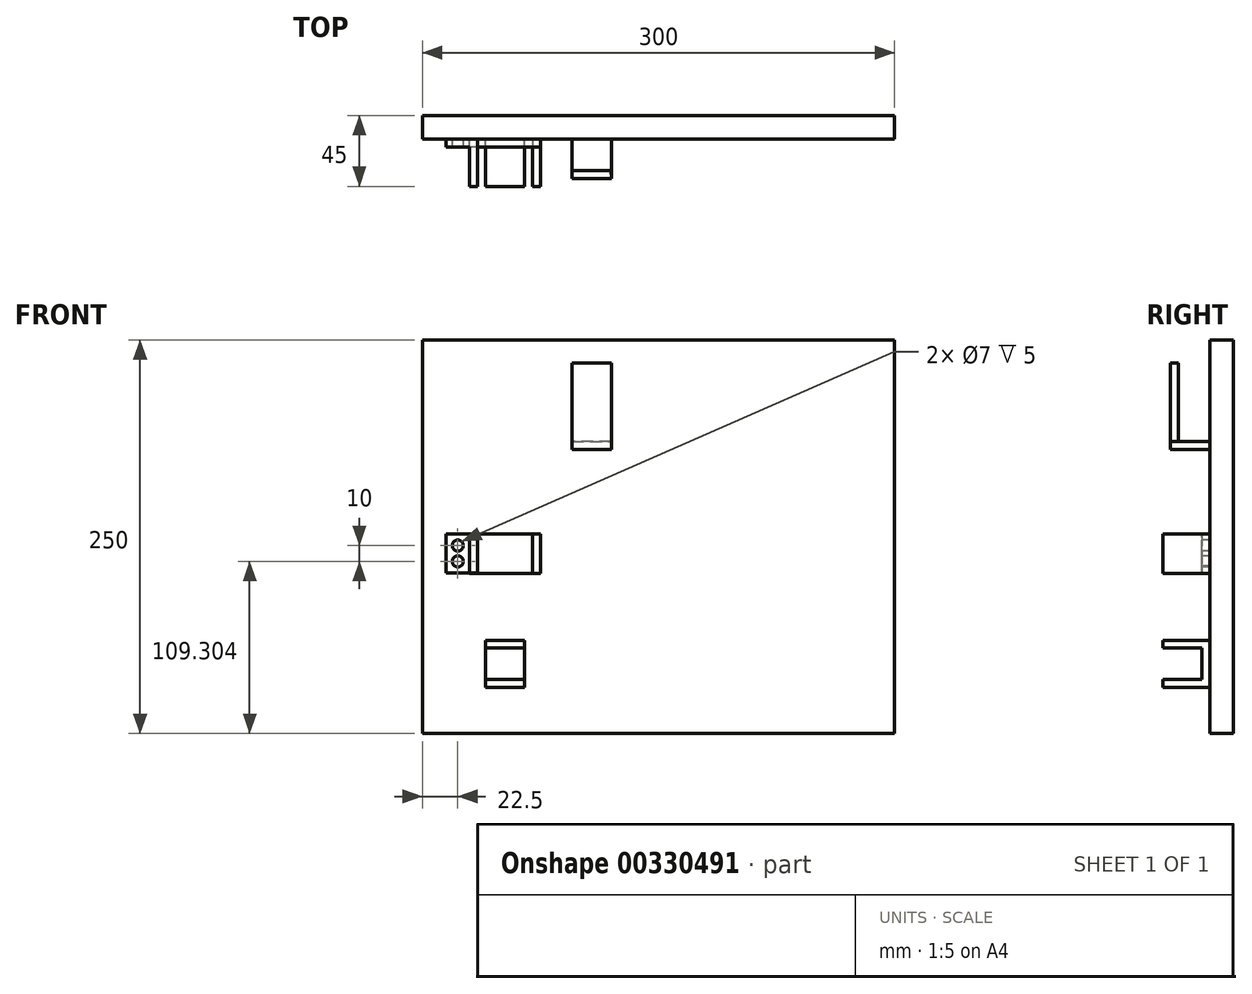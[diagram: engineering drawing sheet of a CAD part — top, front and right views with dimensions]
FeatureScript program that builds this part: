
annotation { "Feature Type Name" : "Feature", "Feature Type Description" : "" }
export const myFeature = defineFeature(function(context is Context, id is Id, definition is map)
    precondition{}
    {
        {
            var Q0;
            Q0=qCreatedBy(makeId("Front.planeOp"),FACE);
            var sketch = newSketch(context, id + "F0", { "sketchPlane" : qUnion([Q0])});
            skLineSegment(sketch, "E0", {"start": v(0, 0) * mm, "end": v(300, 0) * mm});
            skLineSegment(sketch, "E1", {"start": v(300, 0) * mm, "end": v(300, -250) * mm});
            skLineSegment(sketch, "E2", {"start": v(300, -250) * mm, "end": v(0, -250) * mm});
            skLineSegment(sketch, "E3", {"start": v(0, -250) * mm, "end": v(0, 0) * mm});
            skSolve(sketch);
        }
        {
            var Q0;
            Q0=makeQuery(id+"F0.imprint","IMPRINT",FACE,{"disambiguationData":[TD([[makeQuery(id+"F0.imprint","IMPRINT",EDGE,{"derivedFrom":sQuery(id+"F0.wireOp",EDGE,"E0")}),-1.0]])]});
            extrude(context, id + "F1", {"entities" : qUnion([Q0]), "oppositeDirection" : true, "depth" : 15 * mm});
        }
        {
            var Q0;
            Q0=qCreatedBy(makeId("Front.planeOp"),FACE);
            var sketch = newSketch(context, id + "F2", { "sketchPlane" : qUnion([Q0])});
            skLineSegment(sketch, "E4", {"start": v(40.68, -249.67) * mm, "end": v(40.68, -148.2) * mm, "construction": true});
            skLineSegment(sketch, "E5", {"start": v(40.68, -148.2) * mm, "end": v(0, -148.2) * mm, "construction": true});
            skLineSegment(sketch, "E6", {"start": v(0, -148.2) * mm, "end": v(30, -148.2) * mm, "construction": true});
            skLineSegment(sketch, "E7", {"start": v(30, -148.2) * mm, "end": v(105, -148.2) * mm, "construction": true});
            skLineSegment(sketch, "E8", {"start": v(30, -148.2) * mm, "end": v(15, -148.2) * mm});
            skLineSegment(sketch, "E9", {"start": v(15, -148.2) * mm, "end": v(15, -123.2) * mm});
            skLineSegment(sketch, "E10", {"start": v(15, -123.2) * mm, "end": v(30, -123.2) * mm});
            skLineSegment(sketch, "E11", {"start": v(30, -123.2) * mm, "end": v(30, -148.2) * mm});
            skSolve(sketch);
        }
        {
            var Q0;
            Q0 = qSketchRegion(id + "F2", true);
            extrude(context, id + "F3", {"entities" : qUnion([Q0]), "operationType" : NewBodyOperationType.ADD, "depth" : 5 * mm});
        }
        {
            var Q0;
            Q0=makeQuery(id+"F3.opExtrude","CAP_FACE",FACE,{"disambiguationData":[OSD([sQuery(id+"F2.wireOp",EDGE,"E8"),sQuery(id+"F2.wireOp",EDGE,"E9"),sQuery(id+"F2.wireOp",EDGE,"E10"),sQuery(id+"F2.wireOp",EDGE,"E11")])],"isStart":false});
            var sketch = newSketch(context, id + "F4", { "sketchPlane" : qUnion([Q0])});
            skPoint(sketch, "E12.endSnap0", {"position": v(22.5, -123.2) * mm});
            skPoint(sketch, "E12.end.orphan", {"position": v(22.5, -138.2) * mm});
            skPoint(sketch, "E12.start.orphan", {"position": v(22.5, -148.2) * mm});
            skCircle(sketch, "E13", {"center": v(22.5, -130.7) * mm, "radius": 3.5 * mm});
            skCircle(sketch, "E14", {"center": v(22.5, -140.7) * mm, "radius": 3.5 * mm});
            skSolve(sketch);
        }
        {
            var Q0;
            Q0 = qSketchRegion(id + "F4", true);
            extrude(context, id + "F5", {"entities" : qUnion([Q0]), "operationType" : NewBodyOperationType.REMOVE, "oppositeDirection" : true, "depth" : 5 * mm});
        }
        {
            var Q0;
            Q0=qCreatedBy(makeId("Front.planeOp"),FACE);
            var sketch = newSketch(context, id + "F6", { "sketchPlane" : qUnion([Q0])});
            skLineSegment(sketch, "E15", {"start": v(29.99, -123.2) * mm, "end": v(34.99, -123.2) * mm});
            skLineSegment(sketch, "E16", {"start": v(34.99, -123.2) * mm, "end": v(34.99, -148.2) * mm});
            skLineSegment(sketch, "E17", {"start": v(34.99, -148.2) * mm, "end": v(30, -148.2) * mm});
            skLineSegment(sketch, "E18", {"start": v(30, -148.2) * mm, "end": v(29.99, -123.2) * mm});
            skSolve(sketch);
        }
        {
            var Q0;
            Q0=makeQuery(id+"F6.imprint","IMPRINT",FACE,{"disambiguationData":[TD([[makeQuery(id+"F6.imprint","IMPRINT",EDGE,{"derivedFrom":sQuery(id+"F6.wireOp",EDGE,"E15")}),-1.0]])]});
            extrude(context, id + "F7", {"entities" : qUnion([Q0]), "operationType" : NewBodyOperationType.ADD, "depth" : 30 * mm});
        }
        {
            var Q0;
            Q0=qCreatedBy(makeId("Front.planeOp"),FACE);
            var sketch = newSketch(context, id + "F8", { "sketchPlane" : qUnion([Q0])});
            skLineSegment(sketch, "E19", {"start": v(75.06, -123.42) * mm, "end": v(70.06, -123.42) * mm});
            skPoint(sketch, "E20.orphan", {"position": v(0, -147.66) * mm});
            skLineSegment(sketch, "E21", {"start": v(75.06, -123.42) * mm, "end": v(75.06, -148.42) * mm});
            skLineSegment(sketch, "E22", {"start": v(75.06, -148.42) * mm, "end": v(70.06, -148.42) * mm});
            skLineSegment(sketch, "E23", {"start": v(70.06, -148.42) * mm, "end": v(70.06, -123.42) * mm});
            skSolve(sketch);
        }
        {
            var Q0;
            Q0 = qSketchRegion(id + "F8", true);
            extrude(context, id + "F9", {"entities" : qUnion([Q0]), "operationType" : NewBodyOperationType.ADD, "depth" : 30 * mm});
        }
        {
            var Q0;
            Q0=qCreatedBy(makeId("Front.planeOp"),FACE);
            var sketch = newSketch(context, id + "F10", { "sketchPlane" : qUnion([Q0])});
            skLineSegment(sketch, "E24", {"start": v(30.03, -148.26) * mm, "end": v(30.03, -123.26) * mm});
            skLineSegment(sketch, "E25", {"start": v(30.03, -123.26) * mm, "end": v(75.06, -123.43) * mm});
            skLineSegment(sketch, "E26", {"start": v(75.06, -123.43) * mm, "end": v(75.06, -148.43) * mm});
            skLineSegment(sketch, "E27", {"start": v(75.06, -148.43) * mm, "end": v(30.03, -148.26) * mm});
            skSolve(sketch);
        }
        {
            var Q0;
            Q0 = qSketchRegion(id + "F10", true);
            extrude(context, id + "F11", {"entities" : qUnion([Q0]), "operationType" : NewBodyOperationType.ADD, "depth" : 5 * mm});
        }
        {
            var Q0;
            Q0=qCreatedBy(makeId("Front.planeOp"),FACE);
            var sketch = newSketch(context, id + "F12", { "sketchPlane" : qUnion([Q0])});
            skLineSegment(sketch, "E28", {"start": v(95, -69.65) * mm, "end": v(120, -69.65) * mm});
            skLineSegment(sketch, "E29", {"start": v(120, -69.65) * mm, "end": v(120, -64.65) * mm});
            skLineSegment(sketch, "E30", {"start": v(120, -64.65) * mm, "end": v(95, -64.65) * mm});
            skPoint(sketch, "E31.start.orphan", {"position": v(0, -69.65) * mm});
            skPoint(sketch, "E32.end.orphan", {"position": v(95.34, -69.65) * mm});
            skLineSegment(sketch, "E33", {"start": v(95, -64.65) * mm, "end": v(95, -69.65) * mm});
            skSolve(sketch);
        }
        {
            var Q0;
            Q0 = qSketchRegion(id + "F12", true);
            extrude(context, id + "F13", {"entities" : qUnion([Q0]), "operationType" : NewBodyOperationType.ADD, "depth" : 25 * mm});
        }
        {
            var Q0;
            Q0=makeQuery(id+"F13.opExtrude","SWEPT_FACE",FACE,{"disambiguationData":[OSD([sQuery(id+"F12.wireOp",EDGE,"E30")])]});
            var sketch = newSketch(context, id + "F14", { "sketchPlane" : qUnion([Q0])});
            skLineSegment(sketch, "E34", {"start": v(119.96, -25) * mm, "end": v(119.96, -20) * mm});
            skLineSegment(sketch, "E35", {"start": v(95, -25) * mm, "end": v(95, -20) * mm});
            skLineSegment(sketch, "E36", {"start": v(95, -25) * mm, "end": v(120, -25) * mm});
            skLineSegment(sketch, "E37", {"start": v(120, -25) * mm, "end": v(119.96, -20) * mm});
            skLineSegment(sketch, "E38", {"start": v(95, -20) * mm, "end": v(119.96, -20) * mm});
            skSolve(sketch);
        }
        {
            var Q0;
            Q0 = qSketchRegion(id + "F14", true);
            var Q1;
            {var subQ0=sQuery(id+"F14.wireOp",EDGE,"E34");Q1=makeQuery(id+"F14.imprint","IMPRINT",FACE,{"disambiguationData":[TD([[makeQuery(id+"F14.imprint","IMPRINT",EDGE,{"derivedFrom":subQ0}),1.0]])]});}
            extrude(context, id + "F15", {"entities" : qUnion([Q0, Q1]), "operationType" : NewBodyOperationType.ADD, "depth" : 50 * mm});
        }
        {
            var Q0;
            Q0=qCreatedBy(makeId("Front.planeOp"),FACE);
            var sketch = newSketch(context, id + "F16", { "sketchPlane" : qUnion([Q0])});
            skLineSegment(sketch, "E39", {"start": v(43.78, -250.8) * mm, "end": v(43.78, -220.8) * mm, "construction": true});
            skLineSegment(sketch, "E40", {"start": v(0, -220.8) * mm, "end": v(40, -220.8) * mm, "construction": true});
            skLineSegment(sketch, "E41.bottom", {"start": v(40, -220.8) * mm, "end": v(65, -220.8) * mm});
            skLineSegment(sketch, "E41.top", {"start": v(40, -190.8) * mm, "end": v(65, -190.8) * mm});
            skLineSegment(sketch, "E41.left", {"start": v(40, -220.8) * mm, "end": v(40, -190.8) * mm});
            skLineSegment(sketch, "E41.right", {"start": v(65, -220.8) * mm, "end": v(65, -190.8) * mm});
            skSolve(sketch);
        }
        {
            var Q0;
            Q0 = qSketchRegion(id + "F16", true);
            extrude(context, id + "F17", {"entities" : qUnion([Q0]), "depth" : 30 * mm});
        }
        {
            var Q0;
            Q0=makeQuery(id+"F17.opExtrude","CAP_FACE",FACE,{"disambiguationData":[OSD([sQuery(id+"F16.wireOp",EDGE,"E41.bottom"),sQuery(id+"F16.wireOp",EDGE,"E41.top"),sQuery(id+"F16.wireOp",EDGE,"E41.left"),sQuery(id+"F16.wireOp",EDGE,"E41.right")])],"isStart":false});
            var sketch = newSketch(context, id + "F18", { "sketchPlane" : qUnion([Q0])});
            skLineSegment(sketch, "E42.bottom", {"start": v(65, -195.68) * mm, "end": v(40, -195.68) * mm});
            skLineSegment(sketch, "E42.top", {"start": v(65, -215.84) * mm, "end": v(40, -215.84) * mm});
            skLineSegment(sketch, "E42.left", {"start": v(65, -195.68) * mm, "end": v(65, -215.84) * mm});
            skLineSegment(sketch, "E42.right", {"start": v(40, -195.68) * mm, "end": v(40, -215.84) * mm});
            skSolve(sketch);
        }
        {
            var Q0;
            Q0 = qSketchRegion(id + "F18", true);
            extrude(context, id + "F19", {"entities" : qUnion([Q0]), "operationType" : NewBodyOperationType.REMOVE, "oppositeDirection" : true, "depth" : 25 * mm});
        }
    });
